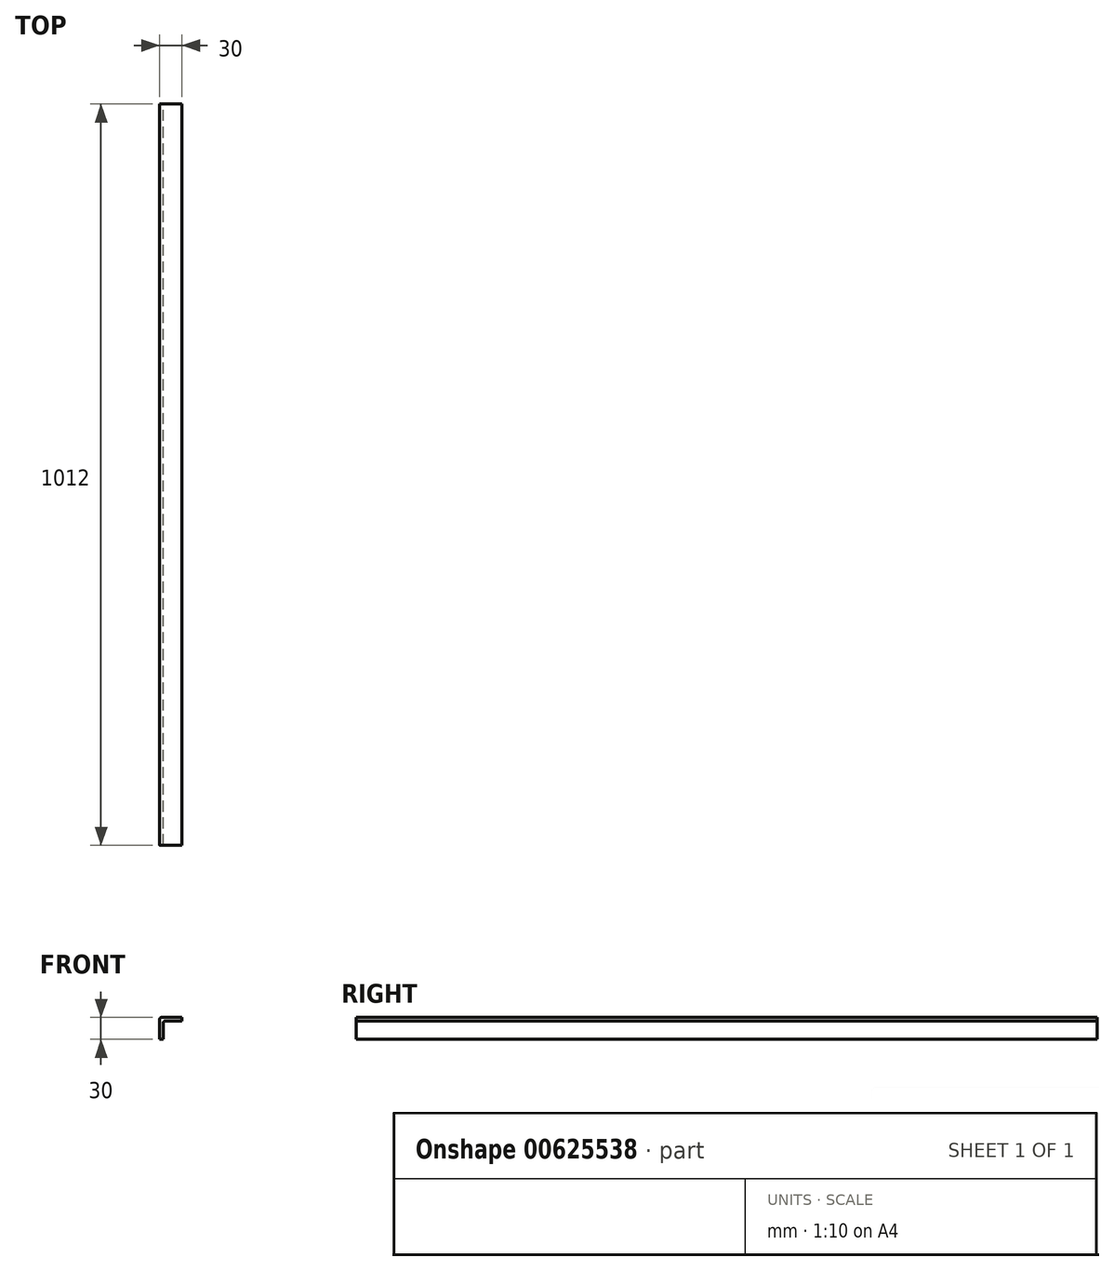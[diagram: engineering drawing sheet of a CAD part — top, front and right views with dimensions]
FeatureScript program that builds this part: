
annotation { "Feature Type Name" : "Feature", "Feature Type Description" : "" }
export const myFeature = defineFeature(function(context is Context, id is Id, definition is map)
    precondition{}
    {
        {
            var Q0;
            Q0=qCreatedBy(makeId("Front.planeOp"),FACE);
            var sketch = newSketch(context, id + "F0", { "sketchPlane" : qUnion([Q0])});
            skLineSegment(sketch, "E0.bottom", {"start": v(-12.5, 15) * mm, "end": v(15, 15) * mm});
            skLineSegment(sketch, "E0.top", {"start": v(-15, -15) * mm, "end": v(-10, -15) * mm});
            skLineSegment(sketch, "E0.left", {"start": v(-15, 12.5) * mm, "end": v(-15, -15) * mm});
            skLineSegment(sketch, "E0.right", {"start": v(15, 15) * mm, "end": v(15, 10) * mm});
            skPoint(sketch, "E0.middle", {"position": v(0, 0) * mm});
            skLineSegment(sketch, "E1", {"start": v(15, 10) * mm, "end": v(-7.5, 10) * mm});
            skLineSegment(sketch, "E2", {"start": v(-10, 7.5) * mm, "end": v(-10, -15) * mm});
            skPoint(sketch, "E3.orphan", {"position": v(15, -15) * mm});
            skPoint(sketch, "E4.visualSharp", {"position": v(-15, 15) * mm});
            skArc(sketch, "E4.filletArc", {"start": v(-12.5, 15) * mm, "mid": v(-14.27, 14.27) * mm, "end": v(-15, 12.5) * mm});
            skPoint(sketch, "E5.visualSharp", {"position": v(-10, 10) * mm});
            skArc(sketch, "E5.filletArc", {"start": v(-7.5, 10) * mm, "mid": v(-9.27, 9.27) * mm, "end": v(-10, 7.5) * mm});
            skSolve(sketch);
        }
        {
            var Q0;
            Q0 = qSketchRegion(id + "F0", true);
            extrude(context, id + "F1", {"entities" : qUnion([Q0]), "depth" : 1012 * mm, "offsetDistance" : 25 * mm});
        }
    });
